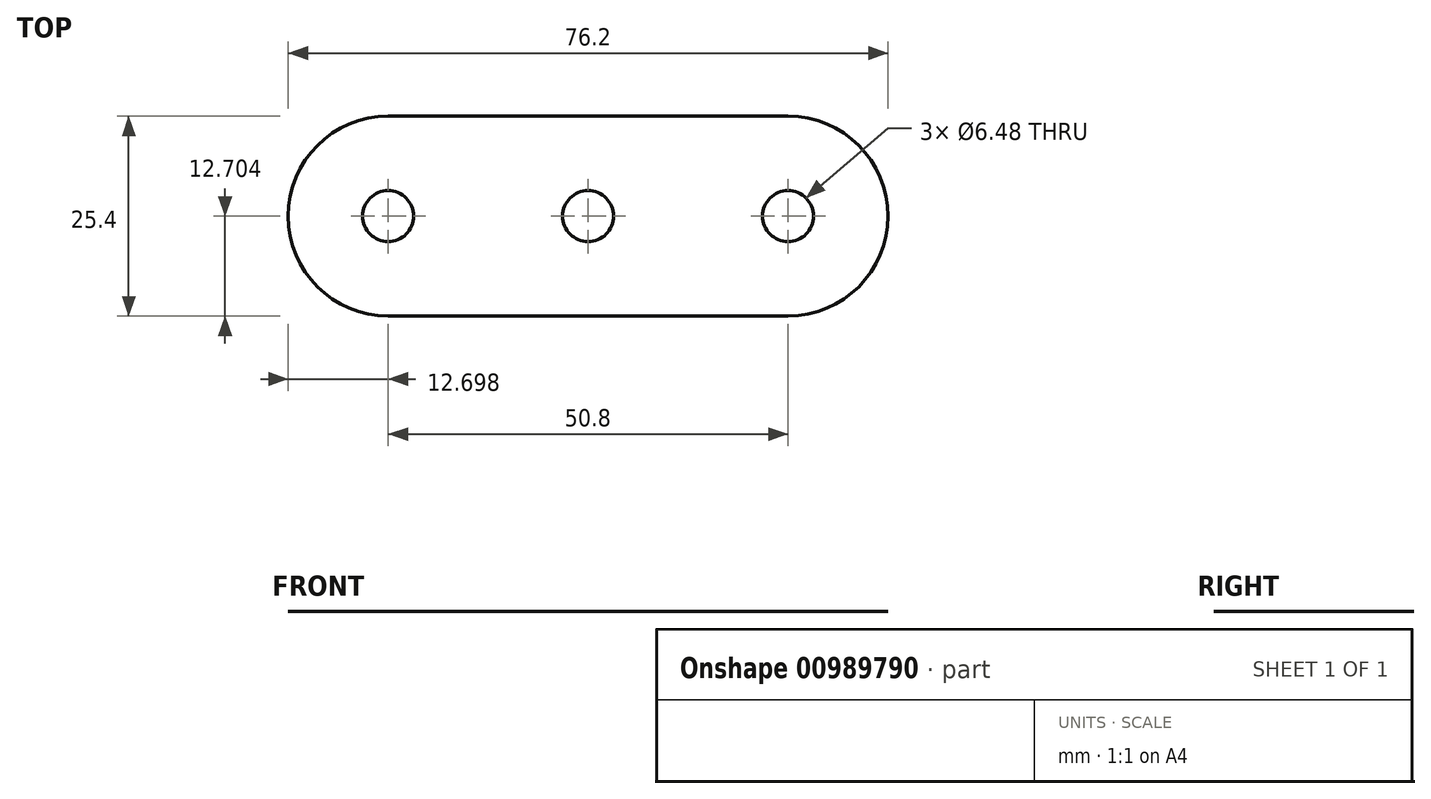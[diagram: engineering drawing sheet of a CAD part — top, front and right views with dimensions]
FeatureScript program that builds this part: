
annotation { "Feature Type Name" : "Feature", "Feature Type Description" : "" }
export const myFeature = defineFeature(function(context is Context, id is Id, definition is map)
    precondition{}
    {
        {
            var Q0;
            Q0=qCreatedBy(makeId("Top.planeOp"),FACE);
            var sketch = newSketch(context, id + "F0", { "sketchPlane" : qUnion([Q0])});
            skLineSegment(sketch, "E0.bottom", {"start": v(-12.74, 8.7) * mm, "end": v(38.06, 8.7) * mm});
            skLineSegment(sketch, "E0.top", {"start": v(-12.74, -16.7) * mm, "end": v(38.06, -16.7) * mm});
            skLineSegment(sketch, "E0.left", {"start": v(-25.44, -4) * mm, "end": v(-25.44, -4) * mm});
            skLineSegment(sketch, "E0.right", {"start": v(50.76, -4) * mm, "end": v(50.76, -4) * mm});
            skPoint(sketch, "E1.visualSharp", {"position": v(-25.44, 8.7) * mm});
            skArc(sketch, "E1.filletArc", {"start": v(-12.74, 8.7) * mm, "mid": v(-21.72, 4.97) * mm, "end": v(-25.44, -4) * mm});
            skPoint(sketch, "E2.visualSharp", {"position": v(-25.44, -16.7) * mm});
            skArc(sketch, "E2.filletArc", {"start": v(-25.44, -4) * mm, "mid": v(-21.72, -12.99) * mm, "end": v(-12.74, -16.7) * mm});
            skPoint(sketch, "E3.visualSharp", {"position": v(50.76, 8.7) * mm});
            skArc(sketch, "E3.filletArc", {"start": v(50.76, -4) * mm, "mid": v(47.04, 4.97) * mm, "end": v(38.06, 8.7) * mm});
            skPoint(sketch, "E4.visualSharp", {"position": v(50.76, -16.7) * mm});
            skArc(sketch, "E4.filletArc", {"start": v(38.06, -16.7) * mm, "mid": v(47.04, -12.99) * mm, "end": v(50.76, -4) * mm});
            skCircle(sketch, "E5", {"center": v(-12.74, -4) * mm, "radius": 3.24 * mm});
            skCircle(sketch, "E6", {"center": v(38.06, -4) * mm, "radius": 3.24 * mm});
            skLineSegment(sketch, "E7", {"start": v(12.66, 8.7) * mm, "end": v(12.66, -16.7) * mm, "construction": true});
            skCircle(sketch, "E8", {"center": v(12.66, -4) * mm, "radius": 3.24 * mm});
            skSolve(sketch);
        }
        {
            var Q0;
            Q0 = qSketchRegion(id + "F0", true);
            extrude(context, id + "F1", {"entities" : qUnion([Q0]), "depth" : 1 / 406.4 * mm, "offsetDistance" : 25.4 * mm});
        }
    });
